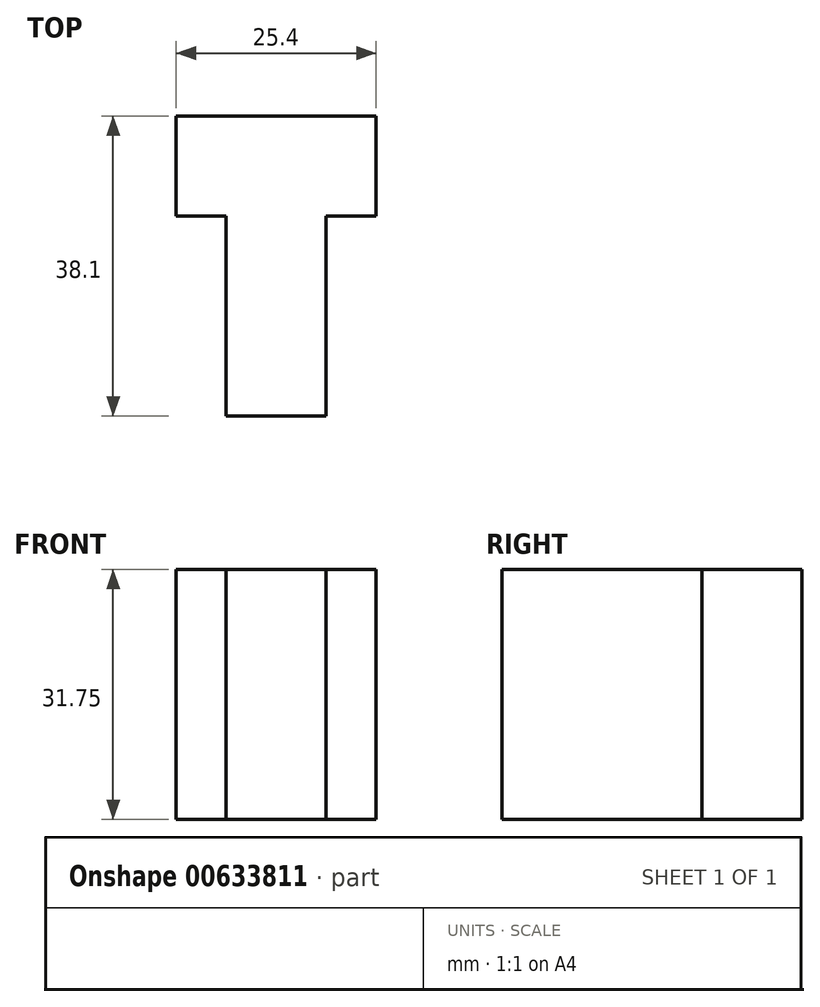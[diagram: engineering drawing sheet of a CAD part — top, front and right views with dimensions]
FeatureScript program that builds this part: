
annotation { "Feature Type Name" : "Feature", "Feature Type Description" : "" }
export const myFeature = defineFeature(function(context is Context, id is Id, definition is map)
    precondition{}
    {
        {
            var Q0;
            Q0=qCreatedBy(makeId("Top.planeOp"),FACE);
            var sketch = newSketch(context, id + "F0", { "sketchPlane" : qUnion([Q0])});
            skLineSegment(sketch, "E0", {"start": v(0, 0) * mm, "end": v(0, 25.4) * mm});
            skLineSegment(sketch, "E1", {"start": v(0, 25.4) * mm, "end": v(6.35, 25.4) * mm});
            skLineSegment(sketch, "E2", {"start": v(6.35, 25.4) * mm, "end": v(6.35, 38.1) * mm});
            skLineSegment(sketch, "E3", {"start": v(6.35, 38.1) * mm, "end": v(-19.05, 38.1) * mm});
            skLineSegment(sketch, "E4", {"start": v(-19.05, 38.1) * mm, "end": v(-19.05, 25.4) * mm});
            skLineSegment(sketch, "E5", {"start": v(-19.05, 25.4) * mm, "end": v(-12.7, 25.4) * mm});
            skLineSegment(sketch, "E6", {"start": v(-12.7, 25.4) * mm, "end": v(-12.7, 0) * mm});
            skLineSegment(sketch, "E7", {"start": v(-12.7, 0) * mm, "end": v(0, 0) * mm});
            skSolve(sketch);
        }
        {
            var Q0;
            Q0=makeQuery(id+"F0.imprint","IMPRINT",FACE,{"disambiguationData":[TD([[makeQuery(id+"F0.imprint","IMPRINT",EDGE,{"derivedFrom":sQuery(id+"F0.wireOp",EDGE,"E0")}),1.0]])]});
            extrude(context, id + "F1", {"entities" : qUnion([Q0]), "depth" : 31.75 * mm, "offsetDistance" : 25.4 * mm});
        }
    });
